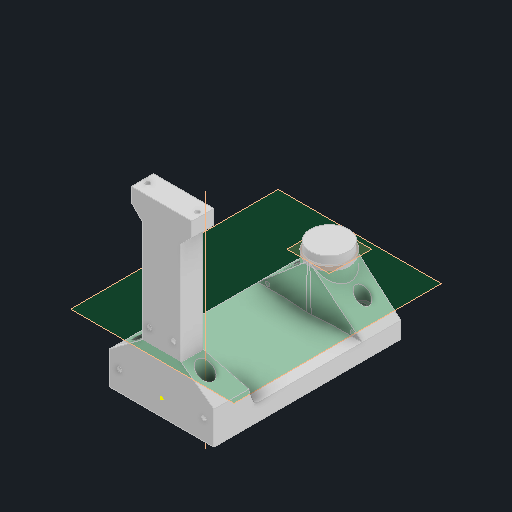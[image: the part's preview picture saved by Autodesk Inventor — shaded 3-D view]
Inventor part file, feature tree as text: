
AUTODESK INVENTOR PART (.ipt)
format: ipt  version: 2023.2 (Build 272271000, 271)  size: 388,096 bytes
history: native  units: in
note: dims shown in document units (in); Inventor stores cm internally (conversion verified against a paired STEP export)
features: sketch x19, extrude x11, mirror x5, thicken_offset x4, other x4, hole x3, loft x2, plane x2, chamfer x2
ambient origin geometry x8: Origin, YZ Plane, XZ Plane, XY Plane, X Axis, Y Axis, Z Axis, Center Point
bodies: Solid1 (feature_tree)
feature tree (52):
  extrude  "Extrusion1"  Depth=1.8898in TaperAngle=0.0deg
  extrude  "Extrusion2"  Depth=0.1969in TaperAngle=0.0deg
  extrude  "Extrusion3"  Depth=5.9055in TaperAngle=0.0deg
  extrude  "Extrusion10"  Depth=0.1181in TaperAngle=0.0deg
  extrude  "Extrusion11"  Depth=0.1575in
  extrude  "Extrusion12"  Depth=1.9685in TaperAngle=0.0deg
  thicken_offset  "Thicken1"
  thicken_offset  "Thicken2"
  loft  "Loft2"
  mirror  "Mirror2"
  extrude  "Extrusion13"  Depth=0.3937in
  plane  "Work Plane2"
  sketch  "Sketch19"  dims[d57=1.5748in d58=0.0in d59=90.0deg]
  thicken_offset  "Thicken5"
  thicken_offset  "Thicken6"
  hole  "Hole1"  [1 undecoded]
  chamfer  "Chamfer1"  Angle=90.0deg  [1 undecoded]
  extrude  "Extrusion18"  Depth=0.1575in
  mirror  "Mirror3"
  extrude  "Extrusion19"  Depth=0.7874in TaperAngle=0.0deg
  loft  "Loft3"
  mirror  "Mirror4"
  sketch  "Sketch28"  dims[d81=0.3937in]
  hole  "Hole2"  [1 undecoded]
  mirror  "Mirror5"
  hole  "Hole3"  [1 undecoded]
  other  "Work Axis1"
  plane  "Work Plane3"
  sketch  "Sketch31"  dims[d115=0.0in d116=90.0deg d117=0.0in d118=90.0deg]
  extrude  "Extrusion20"  Depth=0.3937in TaperAngle=0.0deg
  extrude  "Extrusion21"  TaperAngle=0.0deg  [1 undecoded]
  mirror  "Mirror6"
  chamfer  "Chamfer7"  Distance=0.5906in
  sketch  "Sketch1"  dims[d0=1.378in d1=1.8898in d2=0.0in]
  sketch  "Sketch2"  dims[d3=6.6929in d4=0.1969in d5=0.0in]
  sketch  "Sketch3"  dims[d6=0.7874in d7=5.9055in d8=0.0in]
  sketch  "Sketch10"  dims[d34=2.1654in d35=0.1181in d36=0.0in]
  sketch  "Sketch11"  dims[d37=0.1575in d38=0.1575in]
  sketch  "Sketch12"  dims[d39=0.1181in d40=0.0in d41=1.9685in d42=3.3465in d43=0.0in d44=0.0in]
  sketch  "Sketch13"  dims[d45=0.3937in d46=0.3937in]
  sketch  "Sketch15"  dims[d47=0.3937in d48=0.3937in]
  sketch  "Sketch17"  dims[d49=1.4646in d56=0.7874in]
  sketch  "Sketch22"  dims[d60=0.0in d61=90.0deg d62=0.1575in]
  sketch  "Sketch23"  dims[d63=0.1575in d64=0.7874in d65=0.0in]
  sketch  "Sketch26"  dims[d67=1.4961in d78=0.3937in]
  sketch  "Sketch27"  dims[d79=0.3937in d80=0.3937in]
  sketch  "Sketch29"  dims[d82=0.315in d83=0.2362in d84=0.1575in d85=0.0787in d86=90.0deg d87=0.315in d88=0.0in d89=0.3937in d90=0.0787in d91=45.0deg]
  sketch  "Sketch30"  dims[d111=0.7874in d112=0.0in d113=0.3937in d114=0.0in]
  sketch  "Sketch32"  dims[d119=0.1575in d120=0.2362in d121=0.1575in d122=0.0787in d123=90.0deg d124=0.315in d125=0.0in d126=0.5906in d127=0.7874in d128=0.4724in d129=0.7874in d130=0.2362in d131=0.2362in d132=0.1575in d133=0.0787in d134=90.0deg d135=1.9685in d136=0.0in d137=0.5512in d138=0.4724in d139=1.1024in d140=0.0in d141=1.1024in d142=0.0in d143=0.0551in d144=0.0787in d145=45.0deg d146=-0.2756in]
  parser-record x1  (decoder bookkeeping rows leaked as tree rows — omitted from the tree; the rows remain in map.json)
  other  "turret_assembly.iam"
  other  "horizontal_lower_bearing_holder:1"
note: 5 required parameter values undecoded (feature->parameter linkage not recoverable at this tier; creation-order binding heuristic only, values carry confidence <= 0.55)
note: 1 file-system path scrubbed to <path> (originals preserved in map.json)
